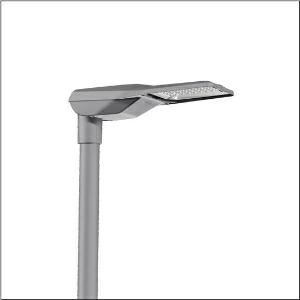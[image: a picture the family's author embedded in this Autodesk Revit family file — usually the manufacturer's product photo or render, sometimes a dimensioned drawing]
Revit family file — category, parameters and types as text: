
# Revit family: streetlight_sl_21_mini___st1_0ab_5xe6m33a08jb_5993
name_source: partatom
category: Lighting Fixtures
units: mm (PartAtom-declared; Revit-internal decimal feet)

## family parameters
Cut with Voids When Loaded = No
Host = Face
Light Source = No
Part Type = Normal
Room Calculation Point = No
Round Connector Dimension = Use Diameter
Shared = No

## types (1)
- --- (1 x LED, 11290 lm, 87.3 W, 3000K)
    Apparent Load = 87 VA
    CIE Flux Codes = 40 74 97 100 100
    Color Rendering = 70
    Color Temperature = 3000K
    Default Elevation = 1800 mm
    Description = Streetlight SL 21 mini, mast luminaire, primary light control with lens, of PMMA, primary optical cover: cover, of toughened safety glass, transparent, light distribution: ST1.0aB, light emission: direct distribution, primary light characteristic: asymmetric, installation type: post-top, side-entry, LED, 3G 1.5mm², High Power LED, rated luminous flux: 11.290lm, luminous efficacy: 129lm/W, light colour: 730, colour temperature: 3000K, control: flexible luminous flux parameterisation, time-dependent luminous flux control, constant luminous flux control, overheat protection, mains connection: 230..240V, AC, 50/60Hz, connection cable pre-assembled, cable length: 10,5m, wiring characteristics: H07RN-F, start of lifetime: 87W, end of service life: 90W, reduction: 40W, luminaire housing, of diecast aluminium, powder-coated, Siteco® metallic grey (DB 702S), corrosivity category C5 mid according to DIN EN ISO 12944, please order mast flange separately, inclination adjustable: 0°, 5°, 10°, 15°, sealing non-destructively replaceable, multi-level sealing system, length: 628mm, width: 235mm, height: 110mm, mast flange for spigot size: 42mm (side-entry): 5XC10008XM4, 60/48mm (side-entry/post-top): 5XC10108XM2, 76/60mm (side-entry/post-top): 5XC10108XM1, protection rating (complete): IP66, insulation class (complete): insulation class II (safety insulation), certification: CE, ENEC, ENEC+, VDE, impact resistance: IK09, permissible operating ambient temperature for outdoor applications: -40..+50°C, standard-compliant lighting for roads and squares, packaging unit: 1 piece

Light Distribution: ST1.0aB
    Height = 110 mm
    Lamp = 1 x LED
    Lamp Light Flux = 11290 lm
    Lamp Power = 87.3 W
    Lamp count = 1
    Length = 625 mm
    Luminous efficacy = 129 lm/W
    Manufacturer = Siteco
    ModVariant = No
    Model = 5XE6M33A08JB
    Number of Poles = 1
    OnlyDefault = Yes
    Power Factor = 1
    Product Name = Streetlight SL 21 mini | ST1.0aB
    Product group = mast luminaire | pylon top
    ProductGroupID = 6100
    Protection Class = Protection class II
    Protection Degree = IP 66
    RLX_Detail_Level = 1
    RLX_Emergency_Light_Flux = 0 lm
    RLX_Emergency_Type = 0
    RLX_Emergency_Type_DB = No
    RlxData = <blob elided: 93757 chars, md5=72e29d83>
    Socket = socket
    Standby Power = 0 W
    System Light Flux = 11290 lm
    System Power = 87 W
    Type Comments = factory setting: luminous flux: 100 % | Output Level: 100 % | 915 mA
    Type Image = l_1003519.jpg
    URL = http://relux.com
    VarID = @adj_118469
    Voltage = 0 V
    Weight = 0.00 kg
    Width = 234 mm

## geometry (parser evidence)
native form markers: Blend x4, Sweep x11
no freeform markers — native parametric forms only
